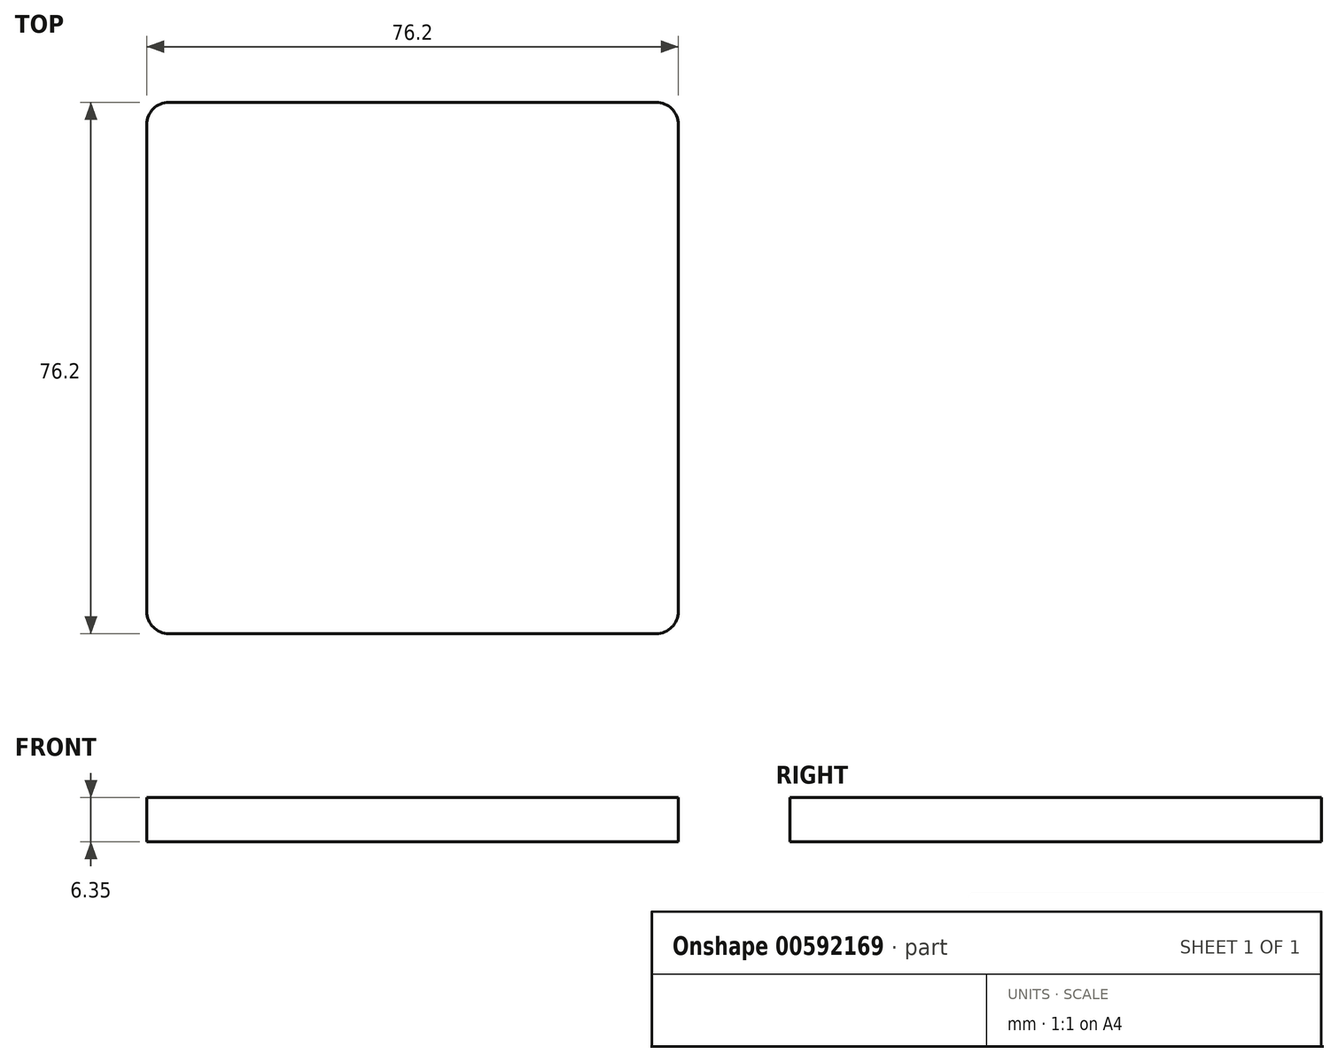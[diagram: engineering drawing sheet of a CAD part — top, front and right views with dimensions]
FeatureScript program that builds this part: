
annotation { "Feature Type Name" : "Feature", "Feature Type Description" : "" }
export const myFeature = defineFeature(function(context is Context, id is Id, definition is map)
    precondition{}
    {
        {
            var Q0;
            Q0=qCreatedBy(makeId("Top.planeOp"),FACE);
            var sketch = newSketch(context, id + "F0", { "sketchPlane" : qUnion([Q0])});
            skLineSegment(sketch, "E0.bottom", {"start": v(34.92, 38.1) * mm, "end": v(-34.93, 38.1) * mm});
            skLineSegment(sketch, "E0.top", {"start": v(34.93, -38.1) * mm, "end": v(-34.92, -38.1) * mm});
            skLineSegment(sketch, "E0.left", {"start": v(38.1, 34.93) * mm, "end": v(38.1, -34.92) * mm});
            skLineSegment(sketch, "E0.right", {"start": v(-38.1, 34.93) * mm, "end": v(-38.1, -34.93) * mm});
            skPoint(sketch, "E0.middle", {"position": v(0, 0) * mm});
            skPoint(sketch, "E1.visualSharp", {"position": v(-38.1, 38.1) * mm});
            skArc(sketch, "E1.filletArc", {"start": v(-34.93, 38.1) * mm, "mid": v(-37.17, 37.17) * mm, "end": v(-38.1, 34.93) * mm});
            skPoint(sketch, "E2.visualSharp", {"position": v(38.1, 38.1) * mm});
            skArc(sketch, "E2.filletArc", {"start": v(38.1, 34.93) * mm, "mid": v(37.17, 37.17) * mm, "end": v(34.92, 38.1) * mm});
            skPoint(sketch, "E3.visualSharp", {"position": v(-38.1, -38.1) * mm});
            skArc(sketch, "E3.filletArc", {"start": v(-38.1, -34.93) * mm, "mid": v(-37.17, -37.17) * mm, "end": v(-34.92, -38.1) * mm});
            skPoint(sketch, "E4.visualSharp", {"position": v(38.1, -38.1) * mm});
            skArc(sketch, "E4.filletArc", {"start": v(34.93, -38.1) * mm, "mid": v(37.17, -37.17) * mm, "end": v(38.1, -34.92) * mm});
            skSolve(sketch);
        }
        {
            var Q0;
            Q0 = qSketchRegion(id + "F0", true);
            extrude(context, id + "F1", {"entities" : qUnion([Q0]), "depth" : 6.35 * mm, "offsetDistance" : 25.4 * mm});
        }
    });
